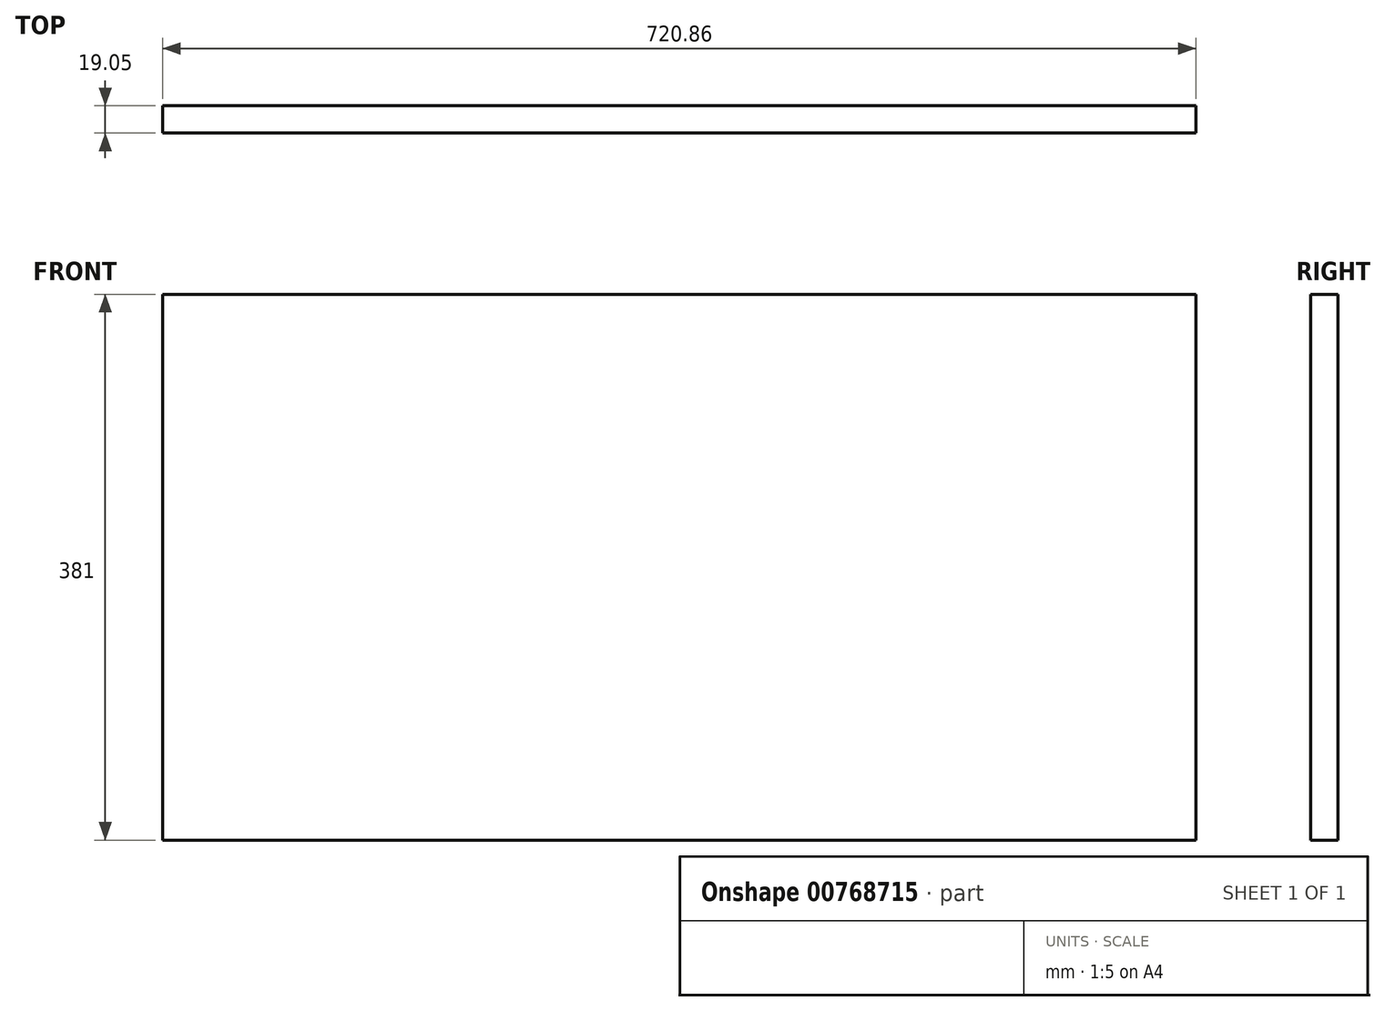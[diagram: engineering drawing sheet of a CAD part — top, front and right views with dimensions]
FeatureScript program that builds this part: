
annotation { "Feature Type Name" : "Feature", "Feature Type Description" : "" }
export const myFeature = defineFeature(function(context is Context, id is Id, definition is map)
    precondition{}
    {
        {
            var Q0;
            Q0=qCreatedBy(makeId("Front.planeOp"),FACE);
            var sketch = newSketch(context, id + "F0", { "sketchPlane" : qUnion([Q0])});
            skLineSegment(sketch, "E0.bottom", {"start": v(-360.43, 190.5) * mm, "end": v(360.43, 190.5) * mm});
            skLineSegment(sketch, "E0.top", {"start": v(-360.43, -190.5) * mm, "end": v(360.43, -190.5) * mm});
            skLineSegment(sketch, "E0.left", {"start": v(-360.43, 190.5) * mm, "end": v(-360.43, -190.5) * mm});
            skLineSegment(sketch, "E0.right", {"start": v(360.43, 190.5) * mm, "end": v(360.43, -190.5) * mm});
            skPoint(sketch, "E0.middle", {"position": v(0, 0) * mm});
            skSolve(sketch);
        }
        {
            var Q0;
            Q0=makeQuery(id+"F0.imprint","IMPRINT",FACE,{"disambiguationData":[TD([[makeQuery(id+"F0.imprint","IMPRINT",EDGE,{"derivedFrom":sQuery(id+"F0.wireOp",EDGE,"E0.bottom")}),-1.0]])]});
            extrude(context, id + "F1", {"entities" : qUnion([Q0]), "depth" : 19.05 * mm, "offsetDistance" : 25.4 * mm});
        }
    });
